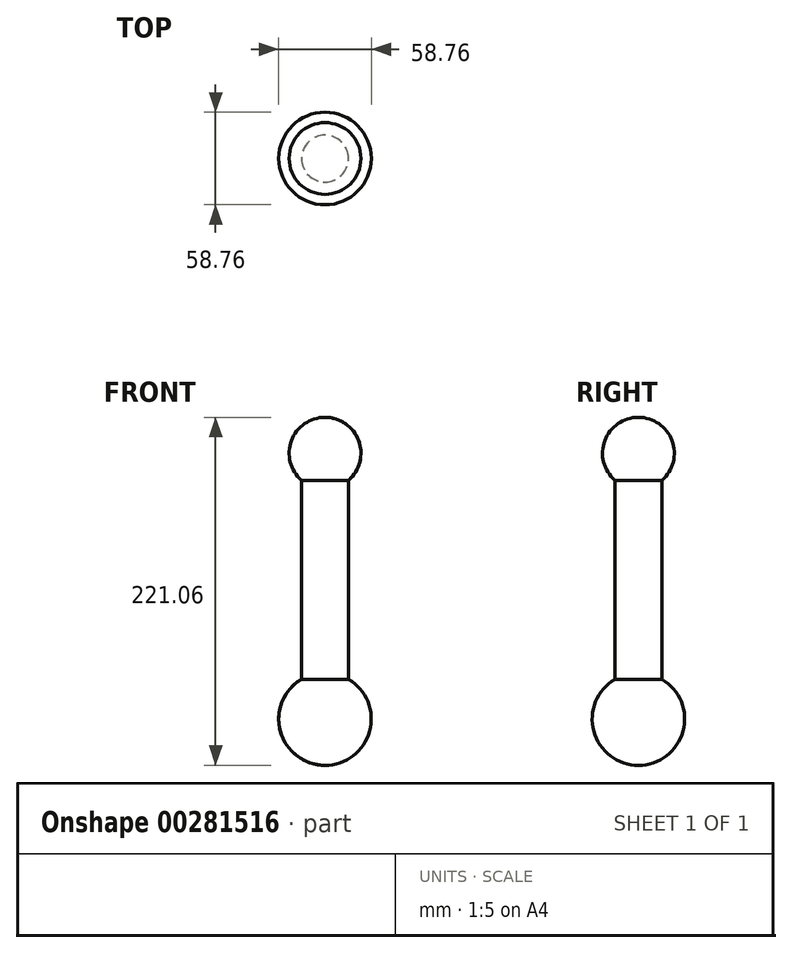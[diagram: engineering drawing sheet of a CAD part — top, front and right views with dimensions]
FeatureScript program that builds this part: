
annotation { "Feature Type Name" : "Feature", "Feature Type Description" : "" }
export const myFeature = defineFeature(function(context is Context, id is Id, definition is map)
    precondition{}
    {
        {
            var Q0;
            Q0=qCreatedBy(makeId("Front.planeOp"),FACE);
            var sketch = newSketch(context, id + "F0", { "sketchPlane" : qUnion([Q0])});
            skLineSegment(sketch, "E0", {"start": v(0, 61.93) * mm, "end": v(0, -159.13) * mm});
            skArc(sketch, "E1", {"start": v(0, 61.93) * mm, "mid": v(-21.36, 47.1) * mm, "end": v(-14.93, 21.9) * mm});
            skLineSegment(sketch, "E2", {"start": v(-14.93, 21.9) * mm, "end": v(-14.93, -104.45) * mm});
            skArc(sketch, "E3", {"start": v(-14.93, -104.45) * mm, "mid": v(-28.34, -137.49) * mm, "end": v(0, -159.13) * mm});
            skSolve(sketch);
        }
        {
            var Q0;
            Q0 = qSketchRegion(id + "F0", true);
            var Q1;
            Q1=sQuery(id+"F0.wireOp",EDGE,"E0");
            revolve(context, id + "F1", {"entities" : qUnion([Q0]), "axis" : qUnion([Q1]), "revolveType" : RevolveType.FULL});
        }
    });
